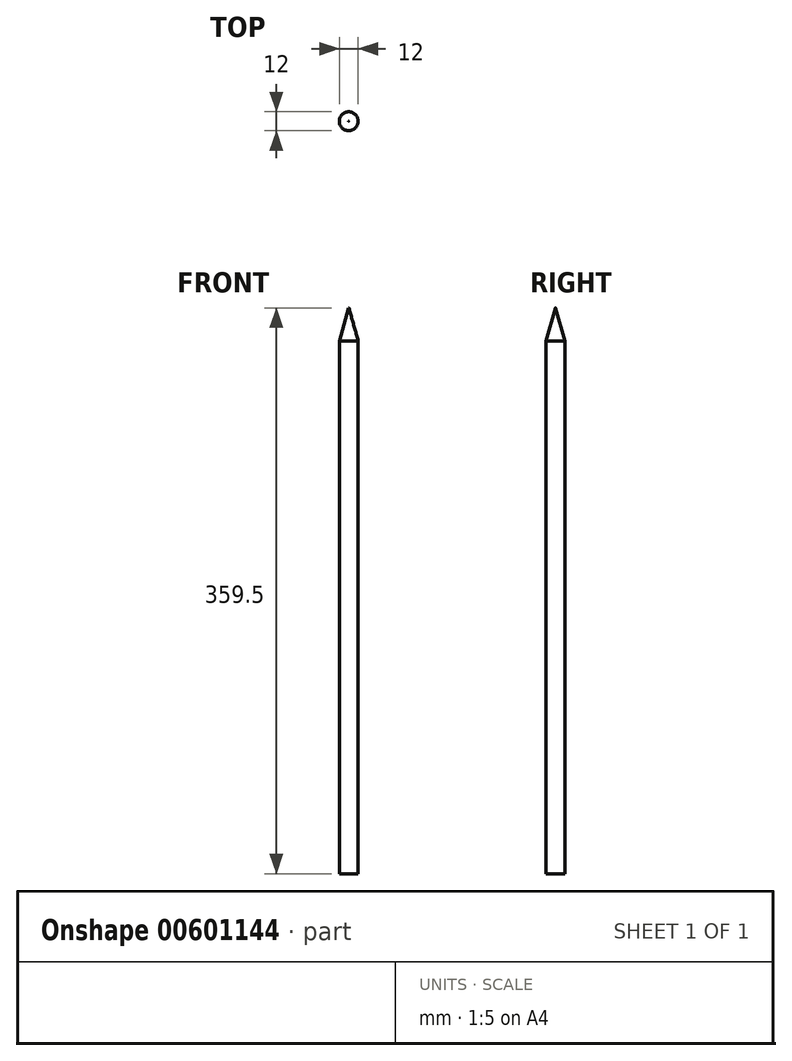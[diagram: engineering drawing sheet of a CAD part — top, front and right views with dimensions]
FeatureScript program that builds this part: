
annotation { "Feature Type Name" : "Feature", "Feature Type Description" : "" }
export const myFeature = defineFeature(function(context is Context, id is Id, definition is map)
    precondition{}
    {
        {
            var Q0;
            Q0=qCreatedBy(makeId("Top.planeOp"),FACE);
            var sketch = newSketch(context, id + "F0", { "sketchPlane" : qUnion([Q0])});
            skCircle(sketch, "E0", {"center": v(0, 0) * mm, "radius": 6 * mm});
            skSolve(sketch);
        }
        {
            var Q0;
            Q0 = qSketchRegion(id + "F0", true);
            extrude(context, id + "F1", {"entities" : qUnion([Q0]), "depth" : 338.5 * mm, "offsetDistance" : 25 * mm});
        }
        {
            var Q0;
            Q0=makeQuery(id+"F1.opExtrude","CAP_FACE",FACE,{"disambiguationData":[OSD([sQuery(id+"F0.wireOp",EDGE,"E0")])],"isStart":false});
            var sketch = newSketch(context, id + "F2", { "sketchPlane" : qUnion([Q0])});
            skCircle(sketch, "E1", {"center": v(0, 0) * mm, "radius": 6 * mm});
            skSolve(sketch);
        }
        {
            var Q0;
            Q0 = qSketchRegion(id + "F2", true);
            extrude(context, id + "F3", {"entities" : qUnion([Q0]), "operationType" : NewBodyOperationType.ADD, "depth" : 21 * mm, "offsetDistance" : 25 * mm, "hasDraft" : true, "draftAngle" : 15.75 * degree, "draftPullDirection" : true});
        }
    });
